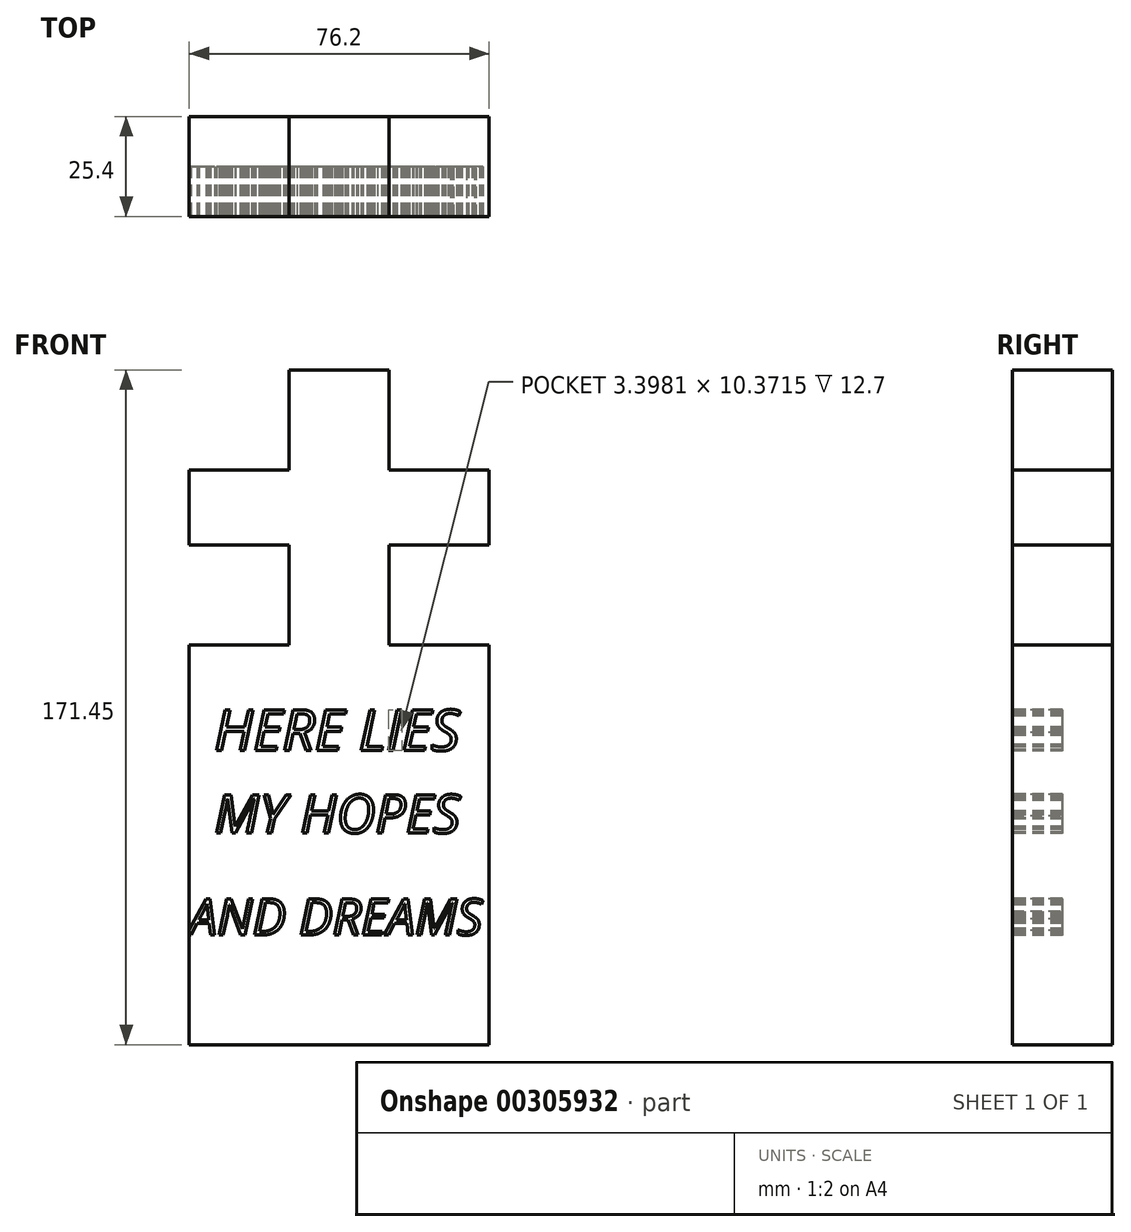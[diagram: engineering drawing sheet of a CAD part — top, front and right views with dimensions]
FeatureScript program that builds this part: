
annotation { "Feature Type Name" : "Feature", "Feature Type Description" : "" }
export const myFeature = defineFeature(function(context is Context, id is Id, definition is map)
    precondition{}
    {
        {
            var Q0;
            Q0=qCreatedBy(makeId("Front.planeOp"),FACE);
            var sketch = newSketch(context, id + "F0", { "sketchPlane" : qUnion([Q0])});
            skLineSegment(sketch, "E0", {"start": v(-38.1, 73.72) * mm, "end": v(-38.1, -27.88) * mm});
            skLineSegment(sketch, "E1.MirrorCS", {"start": v(38.1, 73.72) * mm, "end": v(38.1, -27.88) * mm});
            skLineSegment(sketch, "E2", {"start": v(-38.1, -27.88) * mm, "end": v(38.1, -27.88) * mm});
            skLineSegment(sketch, "E3", {"start": v(-38.1, 73.72) * mm, "end": v(-12.7, 73.72) * mm});
            skLineSegment(sketch, "E4", {"start": v(38.1, 73.72) * mm, "end": v(12.7, 73.72) * mm});
            skLineSegment(sketch, "E5", {"start": v(-12.7, 73.72) * mm, "end": v(-12.7, 99.12) * mm});
            skLineSegment(sketch, "E6", {"start": v(12.7, 73.72) * mm, "end": v(12.7, 99.12) * mm});
            skLineSegment(sketch, "E7", {"start": v(12.7, 99.12) * mm, "end": v(38.1, 99.12) * mm});
            skLineSegment(sketch, "E8", {"start": v(-12.7, 99.12) * mm, "end": v(-38.1, 99.12) * mm});
            skLineSegment(sketch, "E9", {"start": v(-38.1, 99.12) * mm, "end": v(-38.1, 118.17) * mm});
            skLineSegment(sketch, "E10", {"start": v(38.1, 99.12) * mm, "end": v(38.1, 118.17) * mm});
            skLineSegment(sketch, "E11", {"start": v(-38.1, 118.17) * mm, "end": v(-12.7, 118.17) * mm});
            skLineSegment(sketch, "E12", {"start": v(38.1, 118.17) * mm, "end": v(12.7, 118.17) * mm});
            skLineSegment(sketch, "E13", {"start": v(-12.7, 118.17) * mm, "end": v(-12.7, 143.57) * mm});
            skLineSegment(sketch, "E14", {"start": v(12.7, 118.17) * mm, "end": v(12.7, 143.57) * mm});
            skLineSegment(sketch, "E15", {"start": v(-12.7, 143.57) * mm, "end": v(12.7, 143.57) * mm});
            skSolve(sketch);
        }
        {
            var Q0;
            Q0 = qSketchRegion(id + "F0", true);
            extrude(context, id + "F1", {"entities" : qUnion([Q0]), "depth" : 25.4 * mm});
        }
        {
            var Q0;
            Q0=makeQuery(id+"F1.opExtrude","CAP_FACE",FACE,{"disambiguationData":[OSD([sQuery(id+"F0.wireOp",EDGE,"E0"),sQuery(id+"F0.wireOp",EDGE,"E1.MirrorCS"),sQuery(id+"F0.wireOp",EDGE,"E2"),sQuery(id+"F0.wireOp",EDGE,"E3"),sQuery(id+"F0.wireOp",EDGE,"E4"),sQuery(id+"F0.wireOp",EDGE,"E5"),sQuery(id+"F0.wireOp",EDGE,"E6"),sQuery(id+"F0.wireOp",EDGE,"E7"),sQuery(id+"F0.wireOp",EDGE,"E8"),sQuery(id+"F0.wireOp",EDGE,"E9"),sQuery(id+"F0.wireOp",EDGE,"E10"),sQuery(id+"F0.wireOp",EDGE,"E11"),sQuery(id+"F0.wireOp",EDGE,"E12"),sQuery(id+"F0.wireOp",EDGE,"E13"),sQuery(id+"F0.wireOp",EDGE,"E14"),sQuery(id+"F0.wireOp",EDGE,"E15")])],"isStart":false});
            var sketch = newSketch(context, id + "F2", { "sketchPlane" : qUnion([Q0])});
            skText(sketch, "E16", { "text": "HERE LIES", "fontName": "OpenSans-Italic.ttf"});
            skText(sketch, "E17", { "text": "MY HOPES", "fontName": "OpenSans-Italic.ttf"});
            skText(sketch, "E18", { "text": "AND DREAMS", "fontName": "OpenSans-Italic.ttf"});
            const initialGuessF2  = {"E16": [-0.03175, 0.04683, 1, 0, 0.01046], "E17": [-0.03175, 0.02589, 1, 0, 0.00982], "E18": [-0.0381, 0, 1, 0, 0.0092]};
            skSetInitialGuess(sketch, initialGuessF2);
            skSolve(sketch);
        }
        {
            var Q0;
            Q0 = qSketchRegion(id + "F2", true);
            extrude(context, id + "F3", {"entities" : qUnion([Q0]), "operationType" : NewBodyOperationType.REMOVE, "oppositeDirection" : true, "depth" : 12.7 * mm});
        }
    });
